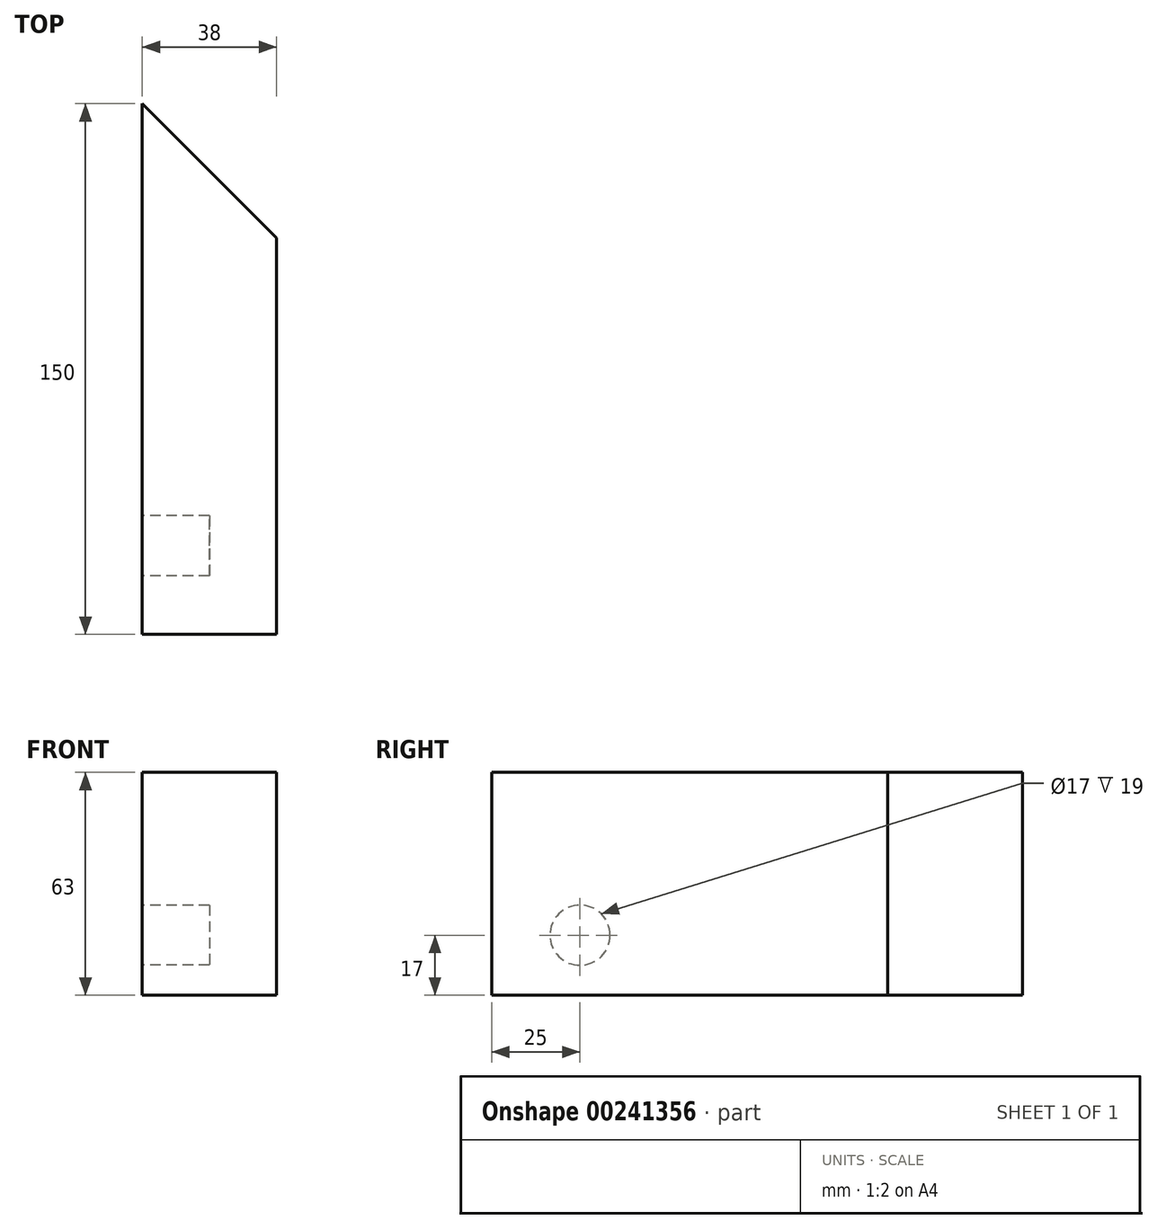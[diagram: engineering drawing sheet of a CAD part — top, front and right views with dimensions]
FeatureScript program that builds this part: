
annotation { "Feature Type Name" : "Feature", "Feature Type Description" : "" }
export const myFeature = defineFeature(function(context is Context, id is Id, definition is map)
    precondition{}
    {
        {
            var Q0;
            Q0=qCreatedBy(makeId("Top.planeOp"),FACE);
            var sketch = newSketch(context, id + "F0", { "sketchPlane" : qUnion([Q0])});
            skLineSegment(sketch, "E0", {"start": v(0, 0) * mm, "end": v(0, 112) * mm});
            skLineSegment(sketch, "E1", {"start": v(0, 112) * mm, "end": v(-38, 150) * mm});
            skLineSegment(sketch, "E2", {"start": v(-38, 150) * mm, "end": v(-38, 0) * mm});
            skLineSegment(sketch, "E3", {"start": v(-38, 0) * mm, "end": v(0, 0) * mm});
            skSolve(sketch);
        }
        {
            var Q0;
            Q0 = qSketchRegion(id + "F0", true);
            extrude(context, id + "F1", {"entities" : qUnion([Q0]), "depth" : 63 * mm});
        }
        {
            var Q0;
            Q0=makeQuery(id+"F1.opExtrude","SWEPT_FACE",FACE,{"disambiguationData":[OSD([sQuery(id+"F0.wireOp",EDGE,"E2")])]});
            var sketch = newSketch(context, id + "F2", { "sketchPlane" : qUnion([Q0])});
            skCircle(sketch, "E4", {"center": v(-25, 17) * mm, "radius": 8.5 * mm});
            skSolve(sketch);
        }
        {
            var Q0;
            Q0 = qSketchRegion(id + "F2", true);
            extrude(context, id + "F3", {"entities" : qUnion([Q0]), "operationType" : NewBodyOperationType.REMOVE, "oppositeDirection" : true, "depth" : 19 * mm});
        }
    });
